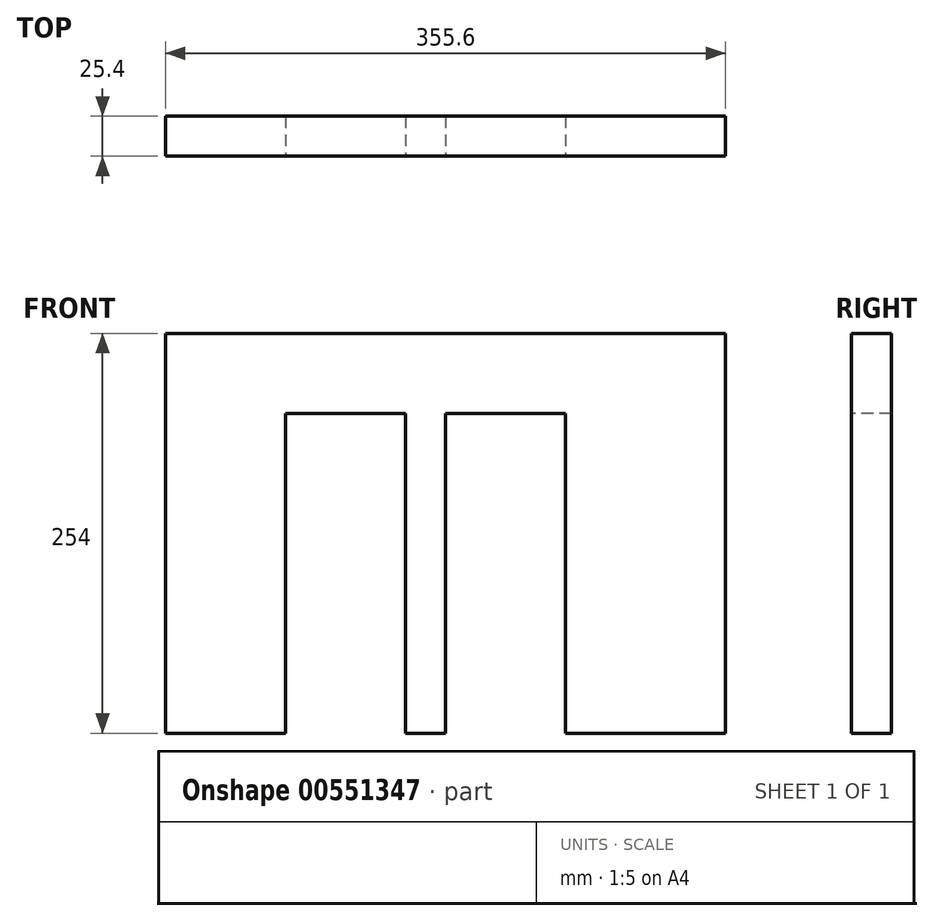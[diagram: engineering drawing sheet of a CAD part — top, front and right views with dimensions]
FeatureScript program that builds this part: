
annotation { "Feature Type Name" : "Feature", "Feature Type Description" : "" }
export const myFeature = defineFeature(function(context is Context, id is Id, definition is map)
    precondition{}
    {
        {
            var Q0;
            Q0=qCreatedBy(makeId("Front.planeOp"),FACE);
            var sketch = newSketch(context, id + "F0", { "sketchPlane" : qUnion([Q0])});
            skLineSegment(sketch, "E0.bottom", {"start": v(-186.06, 135.06) * mm, "end": v(169.54, 135.06) * mm});
            skLineSegment(sketch, "E0.top", {"start": v(-186.06, -118.94) * mm, "end": v(169.54, -118.94) * mm});
            skLineSegment(sketch, "E0.left", {"start": v(-186.06, 135.06) * mm, "end": v(-186.06, -118.94) * mm});
            skLineSegment(sketch, "E0.right", {"start": v(169.54, 135.06) * mm, "end": v(169.54, -118.94) * mm});
            skSolve(sketch);
        }
        {
            var Q0;
            Q0=makeQuery(id+"F0.imprint","IMPRINT",FACE,{"disambiguationData":[TD([[makeQuery(id+"F0.imprint","IMPRINT",EDGE,{"derivedFrom":sQuery(id+"F0.wireOp",EDGE,"E0.bottom")}),-1.0]])]});
            extrude(context, id + "F1", {"entities" : qUnion([Q0]), "depth" : 25.4 * mm, "offsetDistance" : 25.4 * mm});
        }
        {
            var Q0;
            Q0=makeQuery(id+"F1.opExtrude","CAP_FACE",FACE,{"disambiguationData":[OSD([sQuery(id+"F0.wireOp",EDGE,"E0.bottom"),sQuery(id+"F0.wireOp",EDGE,"E0.top"),sQuery(id+"F0.wireOp",EDGE,"E0.left"),sQuery(id+"F0.wireOp",EDGE,"E0.right")])],"isStart":false});
            var sketch = newSketch(context, id + "F2", { "sketchPlane" : qUnion([Q0])});
            skLineSegment(sketch, "E1", {"start": v(-33.66, 135.06) * mm, "end": v(-33.66, -118.94) * mm});
            skLineSegment(sketch, "E2.bottom", {"start": v(-109.86, 84.26) * mm, "end": v(-33.66, 84.26) * mm});
            skLineSegment(sketch, "E2.top", {"start": v(-109.86, -118.94) * mm, "end": v(-33.66, -118.94) * mm});
            skLineSegment(sketch, "E2.left", {"start": v(-109.86, 84.26) * mm, "end": v(-109.86, -118.94) * mm});
            skLineSegment(sketch, "E2.right", {"start": v(-33.66, 84.26) * mm, "end": v(-33.66, -118.94) * mm});
            skLineSegment(sketch, "E3.bottom", {"start": v(-8.26, 84.26) * mm, "end": v(67.94, 84.26) * mm});
            skLineSegment(sketch, "E3.top", {"start": v(-8.26, -118.94) * mm, "end": v(67.94, -118.94) * mm});
            skLineSegment(sketch, "E3.left", {"start": v(-8.26, 84.26) * mm, "end": v(-8.26, -118.94) * mm});
            skLineSegment(sketch, "E3.right", {"start": v(67.94, 84.26) * mm, "end": v(67.94, -118.94) * mm});
            skSolve(sketch);
        }
        {
            var Q0;
            Q0 = qSketchRegion(id + "F2", true);
            extrude(context, id + "F3", {"entities" : qUnion([Q0]), "operationType" : NewBodyOperationType.REMOVE, "oppositeDirection" : true, "depth" : 25.4 * mm, "offsetDistance" : 25.4 * mm});
        }
    });
